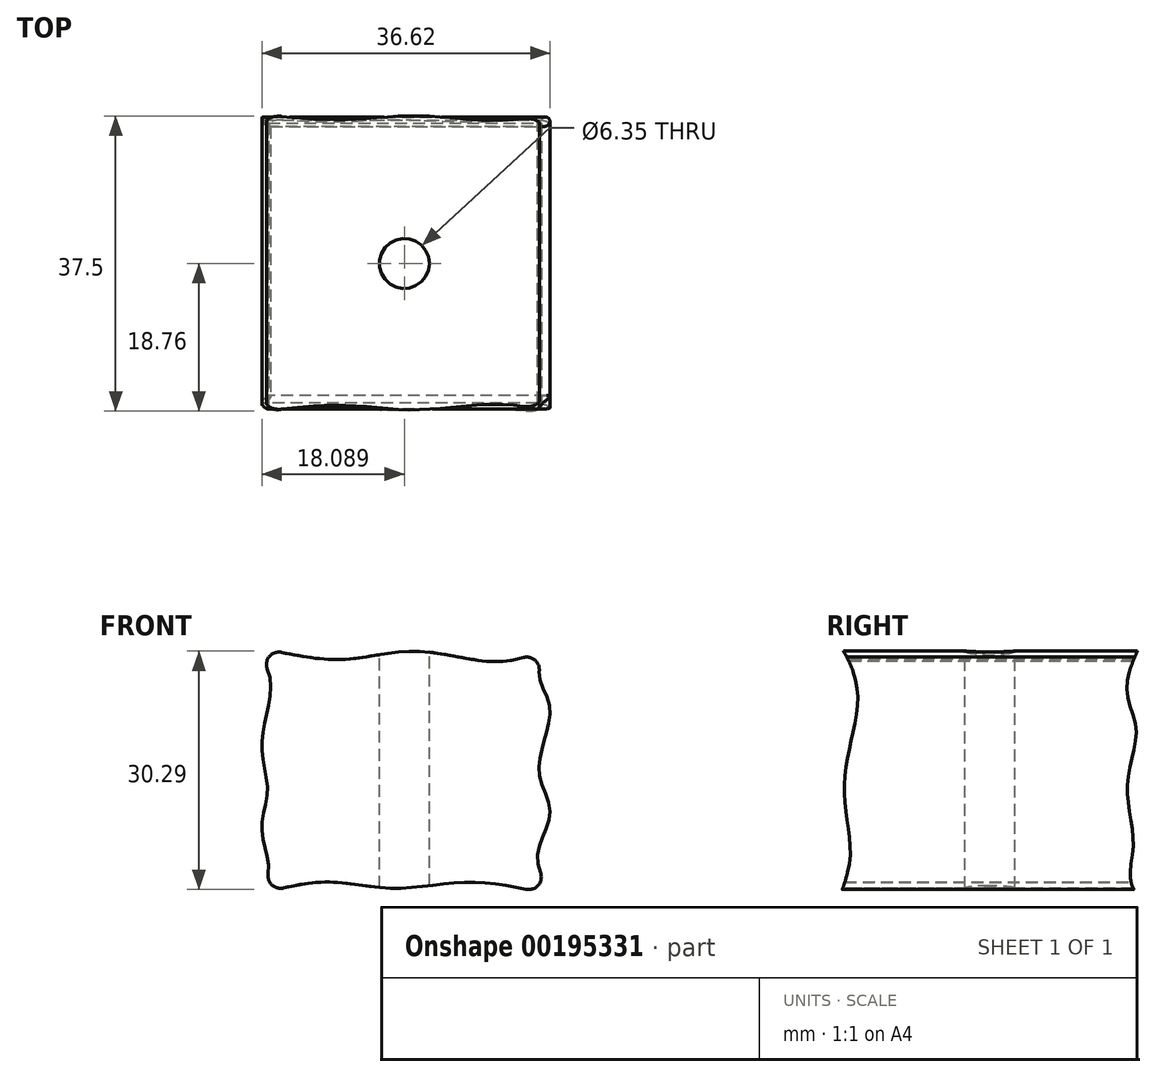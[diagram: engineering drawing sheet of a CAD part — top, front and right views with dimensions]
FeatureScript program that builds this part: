
annotation { "Feature Type Name" : "Feature", "Feature Type Description" : "" }
export const myFeature = defineFeature(function(context is Context, id is Id, definition is map)
    precondition{}
    {
        {
            var Q0;
            Q0=qCreatedBy(makeId("Front.planeOp"),FACE);
            var sketch = newSketch(context, id + "F0", { "sketchPlane" : qUnion([Q0])});
            skLineSegment(sketch, "E0.bottom", {"start": v(0, 0) * mm, "end": v(38.1, 0) * mm});
            skLineSegment(sketch, "E0.top", {"start": v(0, 31.75) * mm, "end": v(38.1, 31.75) * mm});
            skLineSegment(sketch, "E0.left", {"start": v(0, 0) * mm, "end": v(0, 31.75) * mm});
            skLineSegment(sketch, "E0.right", {"start": v(38.1, 0) * mm, "end": v(38.1, 31.75) * mm});
            skSolve(sketch);
        }
        {
            var Q0;
            Q0 = qSketchRegion(id + "F0", true);
            extrude(context, id + "F1", {"entities" : qUnion([Q0]), "endBound" : BoundingType.SYMMETRIC, "depth" : 38.1 * mm});
        }
        {
            var Q0;
            Q0=makeQuery(id+"F1.opExtrude","CAP_FACE",FACE,{"disambiguationData":[OSD([sQuery(id+"F0.wireOp",EDGE,"E0.bottom"),sQuery(id+"F0.wireOp",EDGE,"E0.top"),sQuery(id+"F0.wireOp",EDGE,"E0.left"),sQuery(id+"F0.wireOp",EDGE,"E0.right")])],"isStart":false});
            var sketch = newSketch(context, id + "F2", { "sketchPlane" : qUnion([Q0])});
            skPoint(sketch, "E1.3.internal.snap0", {"position": v(38.1, 15.88) * mm});
            skFitSpline(sketch, "E1", {"points": [v(38.1, 31.75) * mm, v(36.2, 28) * mm, v(37.57, 23.76) * mm, v(36.2, 15.88) * mm, v(37.63, 10.68) * mm, v(36, 5.26) * mm, v(38.1, 0) * mm], "startDerivative": vector(-21.76, -26.47) * mm, "endDerivative": vector(21.46, -31.14) * mm});
            skArc(sketch, "E2", {"start": v(38.1, 0) * mm, "mid": v(41.38, 15.88) * mm, "end": v(38.1, 31.75) * mm});
            skSolve(sketch);
        }
        {
            var Q0;
            {var subQ0=sQuery(id+"F2.wireOp",EDGE,"E1");var subQ1=makeQuery(id+"F1.opExtrude","CAP_EDGE",EDGE,{"disambiguationData":[OSD([sQuery(id+"F0.wireOp",EDGE,"E0.right")])],"isStart":false});var subQ3=makeQuery(id+"F2.imprint","INTERSECT",VERTEX,{"disambiguationData":[OD(0.0)],"derivedFrom":[subQ1,subQ0]});Q0=makeQuery(id+"F2.imprint","IMPRINT",FACE,{"disambiguationData":[TD([[makeQuery(id+"F2.imprint","IMPRINT",EDGE,{"disambiguationData":[TD([[subQ3,1.0]])],"derivedFrom":subQ0}),1.0]])]});}
            var Q1;
            {var subQ0=sQuery(id+"F2.wireOp",EDGE,"E1");var subQ1=makeQuery(id+"F1.opExtrude","CAP_EDGE",EDGE,{"disambiguationData":[OSD([sQuery(id+"F0.wireOp",EDGE,"E0.right")])],"isStart":false});var subQ2=makeQuery(id+"F2.imprint","INTERSECT",VERTEX,{"disambiguationData":[OD(1.0)],"derivedFrom":[subQ1,subQ0]});Q1=makeQuery(id+"F2.imprint","IMPRINT",FACE,{"disambiguationData":[TD([[makeQuery(id+"F2.imprint","IMPRINT",EDGE,{"disambiguationData":[TD([[subQ2,-1.0]])],"derivedFrom":subQ0}),1.0]])]});}
            var Q2;
            {var subQ0=sQuery(id+"F2.wireOp",EDGE,"E1");var subQ1=makeQuery(id+"F1.opExtrude","CAP_EDGE",EDGE,{"disambiguationData":[OSD([sQuery(id+"F0.wireOp",EDGE,"E0.right")])],"isStart":false});var subQ3=makeQuery(id+"F2.imprint","INTERSECT",VERTEX,{"disambiguationData":[OD(3.0)],"derivedFrom":[subQ1,subQ0]});Q2=makeQuery(id+"F2.imprint","IMPRINT",FACE,{"disambiguationData":[TD([[makeQuery(id+"F2.imprint","IMPRINT",EDGE,{"disambiguationData":[TD([[subQ3,-1.0]])],"derivedFrom":subQ0}),1.0]])]});}
            extrude(context, id + "F3", {"entities" : qUnion([Q0, Q1, Q2]), "operationType" : NewBodyOperationType.REMOVE, "endBound" : BoundingType.UP_TO_NEXT, "oppositeDirection" : true, "depth" : 25.4 * mm});
        }
        {
            var Q0;
            Q0=makeQuery(id+"F1.opExtrude","CAP_FACE",FACE,{"disambiguationData":[OSD([sQuery(id+"F0.wireOp",EDGE,"E0.bottom"),sQuery(id+"F0.wireOp",EDGE,"E0.top"),sQuery(id+"F0.wireOp",EDGE,"E0.left"),sQuery(id+"F0.wireOp",EDGE,"E0.right")])],"isStart":false});
            var sketch = newSketch(context, id + "F4", { "sketchPlane" : qUnion([Q0])});
            skFitSpline(sketch, "E3", {"points": [v(0, 31.75) * mm, v(2.12, 26.9) * mm, v(1, 19.54) * mm, v(1.7, 13.29) * mm, v(1, 8.56) * mm, v(1.84, 3) * mm, v(0, 0) * mm], "startDerivative": vector(18.36, -27.31) * mm, "endDerivative": vector(-18.97, -19.65) * mm});
            skArc(sketch, "E4", {"start": v(0, 31.75) * mm, "mid": v(-3.47, 15.88) * mm, "end": v(0, 0) * mm});
            skSolve(sketch);
        }
        {
            var Q0;
            Q0 = qSketchRegion(id + "F4", true);
            extrude(context, id + "F5", {"entities" : qUnion([Q0]), "operationType" : NewBodyOperationType.REMOVE, "oppositeDirection" : true, "depth" : 50.8 * mm});
        }
        {
            var Q0;
            Q0=makeQuery(id+"F1.opExtrude","CAP_FACE",FACE,{"disambiguationData":[OSD([sQuery(id+"F0.wireOp",EDGE,"E0.bottom"),sQuery(id+"F0.wireOp",EDGE,"E0.top"),sQuery(id+"F0.wireOp",EDGE,"E0.left"),sQuery(id+"F0.wireOp",EDGE,"E0.right")])],"isStart":false});
            var sketch = newSketch(context, id + "F6", { "sketchPlane" : qUnion([Q0])});
            skFitSpline(sketch, "E5", {"points": [v(0, 31.75) * mm, v(11.3, 30.03) * mm, v(20.57, 31.08) * mm, v(30.87, 29.75) * mm, v(38.1, 31.75) * mm], "startDerivative": vector(42.77, -10.25) * mm, "endDerivative": vector(30.83, 13.35) * mm});
            skArc(sketch, "E6", {"start": v(38.1, 31.75) * mm, "mid": v(19.05, 34.37) * mm, "end": v(0, 31.75) * mm});
            skSolve(sketch);
        }
        {
            var Q0;
            Q0 = qSketchRegion(id + "F6", true);
            extrude(context, id + "F7", {"entities" : qUnion([Q0]), "operationType" : NewBodyOperationType.REMOVE, "oppositeDirection" : true, "depth" : 50.8 * mm});
        }
        {
            var Q0;
            Q0=makeQuery(id+"F1.opExtrude","CAP_FACE",FACE,{"disambiguationData":[OSD([sQuery(id+"F0.wireOp",EDGE,"E0.bottom"),sQuery(id+"F0.wireOp",EDGE,"E0.top"),sQuery(id+"F0.wireOp",EDGE,"E0.left"),sQuery(id+"F0.wireOp",EDGE,"E0.right")])],"isStart":false});
            var sketch = newSketch(context, id + "F8", { "sketchPlane" : qUnion([Q0])});
            skFitSpline(sketch, "E7", {"points": [v(0, 0) * mm, v(9.23, 1.75) * mm, v(17.77, 0.95) * mm, v(27.5, 1.71) * mm, v(38.1, 0) * mm], "startDerivative": vector(37.81, 10.54) * mm, "endDerivative": vector(40.3, -9.77) * mm});
            skArc(sketch, "E8", {"start": v(0, 0) * mm, "mid": v(19.05, -1.24) * mm, "end": v(38.1, 0) * mm});
            skSolve(sketch);
        }
        {
            var Q0;
            Q0 = qSketchRegion(id + "F8", true);
            extrude(context, id + "F9", {"entities" : qUnion([Q0]), "operationType" : NewBodyOperationType.REMOVE, "oppositeDirection" : true, "depth" : 50.8 * mm});
        }
        {
            var Q0;
            Q0=qCreatedBy(makeId("Top.planeOp"),FACE);
            cPlane(context, id + "F10", {"entities" : qUnion([Q0]), "cplaneType" : CPlaneType.OFFSET, "offset" : 15.88 * mm, "width" : 152.4 * mm, "height" : 152.4 * mm});
        }
        {
            var Q0;
            Q0=qCreatedBy(makeId("Right.planeOp"),FACE);
            cPlane(context, id + "F11", {"entities" : qUnion([Q0]), "cplaneType" : CPlaneType.OFFSET, "offset" : 19.05 * mm, "width" : 152.4 * mm, "height" : 152.4 * mm});
        }
        {
            var Q0;
            Q0=qCreatedBy(id+"F11.planeOp",FACE);
            var sketch = newSketch(context, id + "F12", { "sketchPlane" : qUnion([Q0])});
            skFitSpline(sketch, "E9", {"points": [v(-19.38, 32.38) * mm, v(-16.8, 25.62) * mm, v(-18.47, 14.5) * mm, v(-17.73, 5.5) * mm, v(-19.05, 0) * mm], "startDerivative": vector(15.17, -24.39) * mm, "endDerivative": vector(-9.06, -24.72) * mm});
            skArc(sketch, "E10", {"start": v(-19.38, 32.38) * mm, "mid": v(-20.38, 16.18) * mm, "end": v(-19.05, 0) * mm});
            skFitSpline(sketch, "E11", {"points": [v(19.12, 31.94) * mm, v(17.37, 26.26) * mm, v(18.58, 20.97) * mm, v(17.46, 14.3) * mm, v(18.2, 7.06) * mm, v(17.83, 3.16) * mm, v(19.08, 0) * mm], "startDerivative": vector(-14.8, -33.76) * mm, "endDerivative": vector(25.44, -18.39) * mm});
            skArc(sketch, "E12", {"start": v(19.08, 0) * mm, "mid": v(20.92, 15.97) * mm, "end": v(19.12, 31.94) * mm});
            skSolve(sketch);
        }
        {
            var Q0;
            Q0 = qSketchRegion(id + "F12", true);
            extrude(context, id + "F13", {"entities" : qUnion([Q0]), "operationType" : NewBodyOperationType.REMOVE, "endBound" : BoundingType.SYMMETRIC, "oppositeDirection" : true, "depth" : 50.8 * mm});
        }
        {
            var Q0;
            {var subQ0=sQuery(id+"F4.wireOp",EDGE,"E3");var subQ1=sQuery(id+"F0.wireOp",EDGE,"E0.top");var subQ2=sQuery(id+"F0.wireOp",EDGE,"E0.left");Q0=makeQuery(id+"F7.boolean.opBoolean","MERGE",EDGE,{"derivedFrom":[makeQuery(id+"F5.boolean.opBoolean","MERGE",EDGE,{"derivedFrom":[makeQuery(id+"F1.opExtrude","SWEPT_EDGE",EDGE,{"disambiguationData":[OSD([subQ1,subQ2])]}),makeQuery(id+"F5.opExtrude","SWEPT_EDGE",EDGE,{"disambiguationData":[OSD([subQ1,subQ2,subQ0,sQuery(id+"F4.wireOp",EDGE,"E4")])]})]}),makeQuery(id+"F7.opExtrude","SWEPT_EDGE",EDGE,{"disambiguationData":[OSD([subQ1,subQ0,sQuery(id+"F6.wireOp",EDGE,"E5"),sQuery(id+"F6.wireOp",EDGE,"E6")])]})]});}
            var Q1;
            {var subQ0=sQuery(id+"F2.wireOp",EDGE,"E1");var subQ1=sQuery(id+"F0.wireOp",EDGE,"E0.bottom");var subQ2=sQuery(id+"F0.wireOp",EDGE,"E0.right");Q1=makeQuery(id+"F9.boolean.opBoolean","MERGE",EDGE,{"derivedFrom":[makeQuery(id+"F3.boolean.opBoolean","MERGE",EDGE,{"derivedFrom":[makeQuery(id+"F1.opExtrude","SWEPT_EDGE",EDGE,{"disambiguationData":[OSD([subQ1,subQ2])]}),makeQuery(id+"F3.opExtrude","SWEPT_EDGE",EDGE,{"disambiguationData":[OSD([subQ1,subQ2,subQ0,sQuery(id+"F2.wireOp",EDGE,"E2")])]})]}),makeQuery(id+"F9.opExtrude","SWEPT_EDGE",EDGE,{"disambiguationData":[OSD([subQ1,subQ0,sQuery(id+"F8.wireOp",EDGE,"E7"),sQuery(id+"F8.wireOp",EDGE,"E8")])]})]});}
            var Q2;
            {var subQ0=sQuery(id+"F4.wireOp",EDGE,"E3");var subQ1=sQuery(id+"F0.wireOp",EDGE,"E0.bottom");var subQ2=sQuery(id+"F0.wireOp",EDGE,"E0.left");Q2=makeQuery(id+"F9.boolean.opBoolean","MERGE",EDGE,{"derivedFrom":[makeQuery(id+"F5.boolean.opBoolean","MERGE",EDGE,{"derivedFrom":[makeQuery(id+"F1.opExtrude","SWEPT_EDGE",EDGE,{"disambiguationData":[OSD([subQ1,subQ2])]}),makeQuery(id+"F5.opExtrude","SWEPT_EDGE",EDGE,{"disambiguationData":[OSD([subQ1,subQ2,subQ0,sQuery(id+"F4.wireOp",EDGE,"E4")])]})]}),makeQuery(id+"F9.opExtrude","SWEPT_EDGE",EDGE,{"disambiguationData":[OSD([subQ1,subQ0,sQuery(id+"F8.wireOp",EDGE,"E7"),sQuery(id+"F8.wireOp",EDGE,"E8")])]})]});}
            var Q3;
            {var subQ0=sQuery(id+"F2.wireOp",EDGE,"E1");var subQ1=sQuery(id+"F0.wireOp",EDGE,"E0.top");var subQ2=sQuery(id+"F0.wireOp",EDGE,"E0.right");Q3=makeQuery(id+"F7.boolean.opBoolean","MERGE",EDGE,{"derivedFrom":[makeQuery(id+"F3.boolean.opBoolean","MERGE",EDGE,{"derivedFrom":[makeQuery(id+"F1.opExtrude","SWEPT_EDGE",EDGE,{"disambiguationData":[OSD([subQ1,subQ2])]}),makeQuery(id+"F3.opExtrude","SWEPT_EDGE",EDGE,{"disambiguationData":[OSD([subQ1,subQ2,subQ0,sQuery(id+"F2.wireOp",EDGE,"E2")])]})]}),makeQuery(id+"F7.opExtrude","SWEPT_EDGE",EDGE,{"disambiguationData":[OSD([subQ1,subQ0,sQuery(id+"F6.wireOp",EDGE,"E5"),sQuery(id+"F6.wireOp",EDGE,"E6")])]})]});}
            fillet(context, id + "F14", {"entities" : qUnion([Q0, Q1, Q2, Q3]), "radius" : 1.59 * mm, "tangentPropagation" : true, "allowEdgeOverflow" : false});
        }
        {
            var Q0;
            Q0=qCreatedBy(id+"F10.planeOp",FACE);
            var sketch = newSketch(context, id + "F15", { "sketchPlane" : qUnion([Q0])});
            skCircle(sketch, "E13", {"center": v(19.09, 0) * mm, "radius": 3.17 * mm});
            skSolve(sketch);
        }
        {
            var Q0;
            Q0 = qSketchRegion(id + "F15", true);
            extrude(context, id + "F16", {"entities" : qUnion([Q0]), "operationType" : NewBodyOperationType.REMOVE, "endBound" : BoundingType.SYMMETRIC, "oppositeDirection" : true, "depth" : 50.8 * mm});
        }
    });
